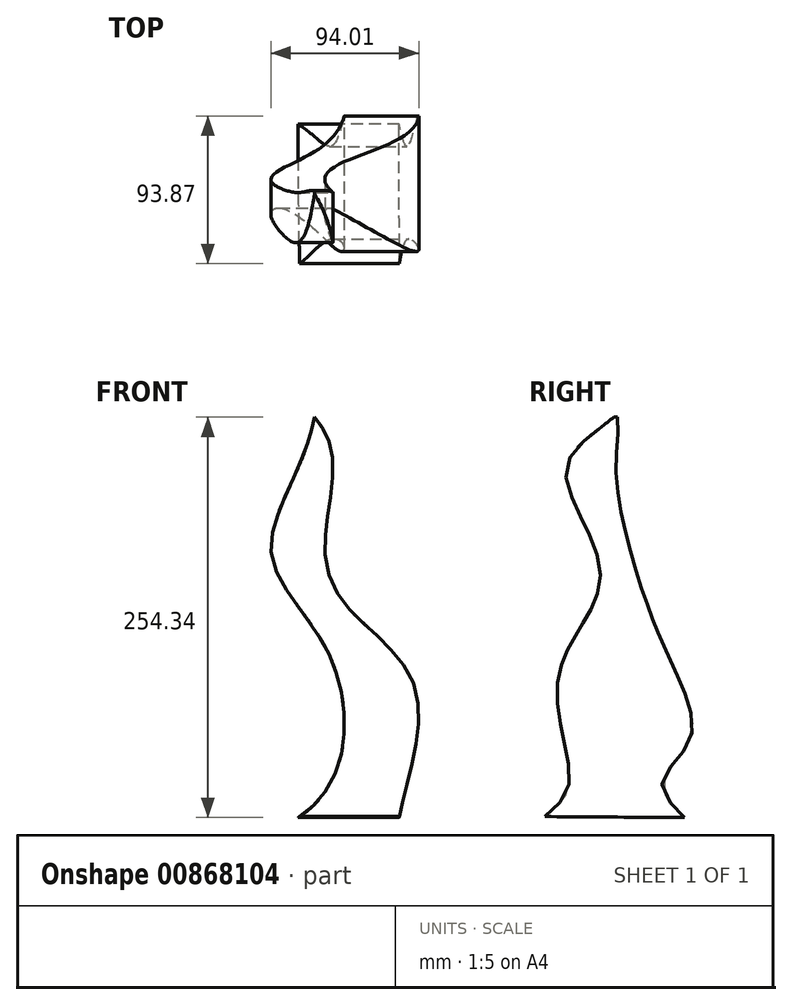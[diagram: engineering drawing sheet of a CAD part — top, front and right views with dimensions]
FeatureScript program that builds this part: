
annotation { "Feature Type Name" : "Feature", "Feature Type Description" : "" }
export const myFeature = defineFeature(function(context is Context, id is Id, definition is map)
    precondition{}
    {
        {
            var Q0;
            Q0=qCreatedBy(makeId("Front.planeOp"),FACE);
            var sketch = newSketch(context, id + "F0", { "sketchPlane" : qUnion([Q0])});
            skFitSpline(sketch, "E0", {"points": [v(-71.38, 125) * mm, v(-98.93, 40.26) * mm, v(-63.7, -22.3) * mm, v(-55.91, -95.24) * mm, v(-83, -130) * mm], "startDerivative": vector(-60.58, -352.8) * mm, "endDerivative": vector(-174.87, -101.54) * mm});
            skFitSpline(sketch, "E1", {"points": [v(-71.38, 125) * mm, v(-63.67, 57.33) * mm, v(-54.33, 9.33) * mm, v(-7.67, -46) * mm, v(-17.67, -130) * mm], "startDerivative": vector(221.18, -243.78) * mm, "endDerivative": vector(-53, -277.24) * mm});
            skLineSegment(sketch, "E2", {"start": v(-83, -130) * mm, "end": v(-17.67, -130) * mm});
            skSolve(sketch);
        }
        {
            var Q0;
            Q0 = qSketchRegion(id + "F0", true);
            extrude(context, id + "F1", {"entities" : qUnion([Q0]), "depth" : 300 * mm, "offsetDistance" : 25 * mm});
        }
        {
            var Q0;
            Q0=qCreatedBy(makeId("Right.planeOp"),FACE);
            var sketch = newSketch(context, id + "F2", { "sketchPlane" : qUnion([Q0])});
            skFitSpline(sketch, "E3", {"points": [v(-176.33, 126.66) * mm, v(-209, 88) * mm, v(-187, 24) * mm, v(-213.67, -39.34) * mm, v(-207, -108) * mm, v(-222.33, -128.67) * mm], "startDerivative": vector(-305.47, -241.49) * mm, "endDerivative": vector(-140.55, -119.38) * mm});
            skFitSpline(sketch, "E4", {"points": [v(-176.33, 126.66) * mm, v(-177, 88) * mm, v(-148.33, -16.67) * mm, v(-129.67, -78.67) * mm, v(-147.67, -106.67) * mm, v(-133.67, -129.34) * mm], "startDerivative": vector(32.76, -238.19) * mm, "endDerivative": vector(156.45, -159.5) * mm});
            skLineSegment(sketch, "E5", {"start": v(-222.33, -128.67) * mm, "end": v(-133.67, -129.34) * mm});
            skSolve(sketch);
        }
        {
            var Q0;
            Q0 = qSketchRegion(id + "F2", true);
            extrude(context, id + "F3", {"entities" : qUnion([Q0]), "depth" : 300 * mm, "offsetDistance" : 25 * mm});
        }
        {
            var Q0;
            Q0=makeQuery(id+"F3.opExtrude","SWEPT_BODY",BODY,{"disambiguationData":[OSD([sQuery(id+"F2.wireOp",EDGE,"E3"),sQuery(id+"F2.wireOp",EDGE,"E4"),sQuery(id+"F2.wireOp",EDGE,"E5")])]});
            transform(context, id + "F4", {"entities" : qUnion([Q0]), "transformType" : TransformType.TRANSLATION_3D, "dx" : -228 * mm, "dy" : 0 * mm, "dz" : 0 * mm, "makeCopy" : false});
        }
        {
            var Q0;
            Q0=makeQuery(id+"F3.opExtrude","SWEPT_BODY",BODY,{"disambiguationData":[OSD([sQuery(id+"F2.wireOp",EDGE,"E3"),sQuery(id+"F2.wireOp",EDGE,"E4"),sQuery(id+"F2.wireOp",EDGE,"E5")])]});
            var Q1;
            Q1=makeQuery(id+"F1.opExtrude","SWEPT_BODY",BODY,{"disambiguationData":[OSD([sQuery(id+"F0.wireOp",EDGE,"E0"),sQuery(id+"F0.wireOp",EDGE,"E1"),sQuery(id+"F0.wireOp",EDGE,"E2")])]});
            booleanBodies(context, id + "F5", {"operationType" : BooleanOperationType.INTERSECTION, "tools" : qUnion([Q0, Q1])});
        }
    });
